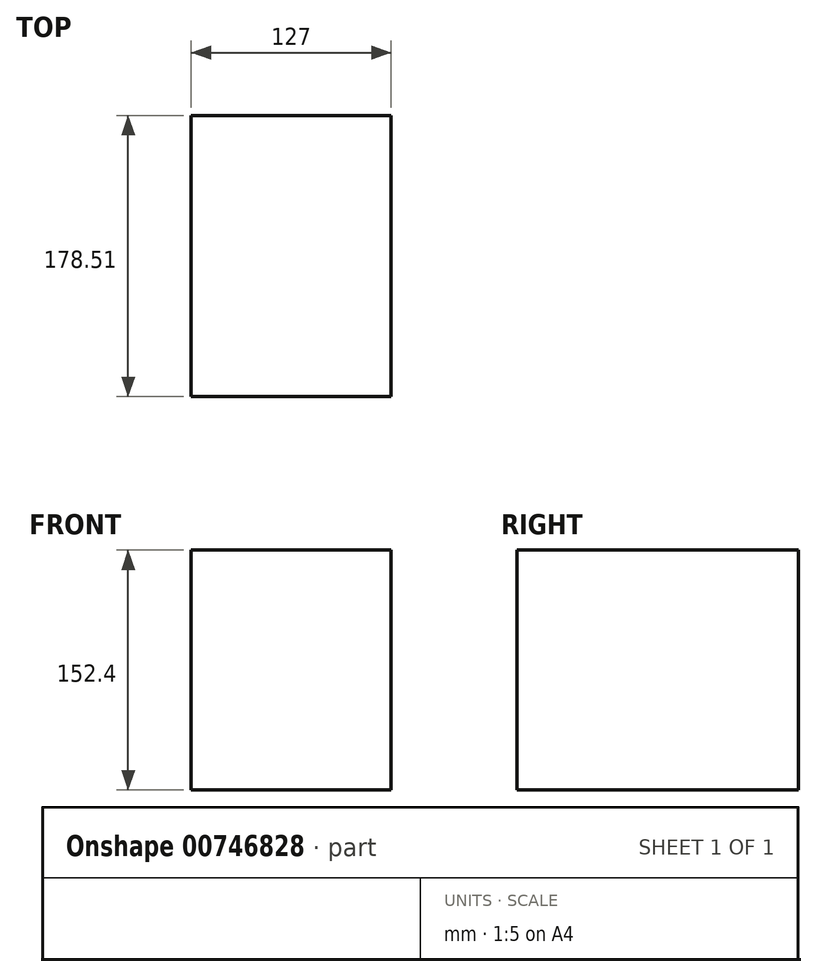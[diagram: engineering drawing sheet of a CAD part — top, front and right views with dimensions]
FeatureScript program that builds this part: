
annotation { "Feature Type Name" : "Feature", "Feature Type Description" : "" }
export const myFeature = defineFeature(function(context is Context, id is Id, definition is map)
    precondition{}
    {
        {
            var Q0;
            Q0=qCreatedBy(makeId("Front.planeOp"),FACE);
            var sketch = newSketch(context, id + "F0", { "sketchPlane" : qUnion([Q0])});
            skLineSegment(sketch, "E0.bottom", {"start": v(63.5, -76.2) * mm, "end": v(-63.5, -76.2) * mm});
            skLineSegment(sketch, "E0.top", {"start": v(63.5, 76.2) * mm, "end": v(-63.5, 76.2) * mm});
            skLineSegment(sketch, "E0.left", {"start": v(63.5, -76.2) * mm, "end": v(63.5, 76.2) * mm});
            skLineSegment(sketch, "E0.right", {"start": v(-63.5, -76.2) * mm, "end": v(-63.5, 76.2) * mm});
            skPoint(sketch, "E0.middle", {"position": v(0, 0) * mm});
            skSolve(sketch);
        }
        {
            var Q0;
            Q0=makeQuery(id+"F0.imprint","IMPRINT",FACE,{"disambiguationData":[TD([[makeQuery(id+"F0.imprint","IMPRINT",EDGE,{"derivedFrom":sQuery(id+"F0.wireOp",EDGE,"E0.bottom")}),-1.0]])]});
            extrude(context, id + "F1", {"entities" : qUnion([Q0]), "depth" : 178.5 * mm, "offsetDistance" : 25.4 * mm});
        }
    });
